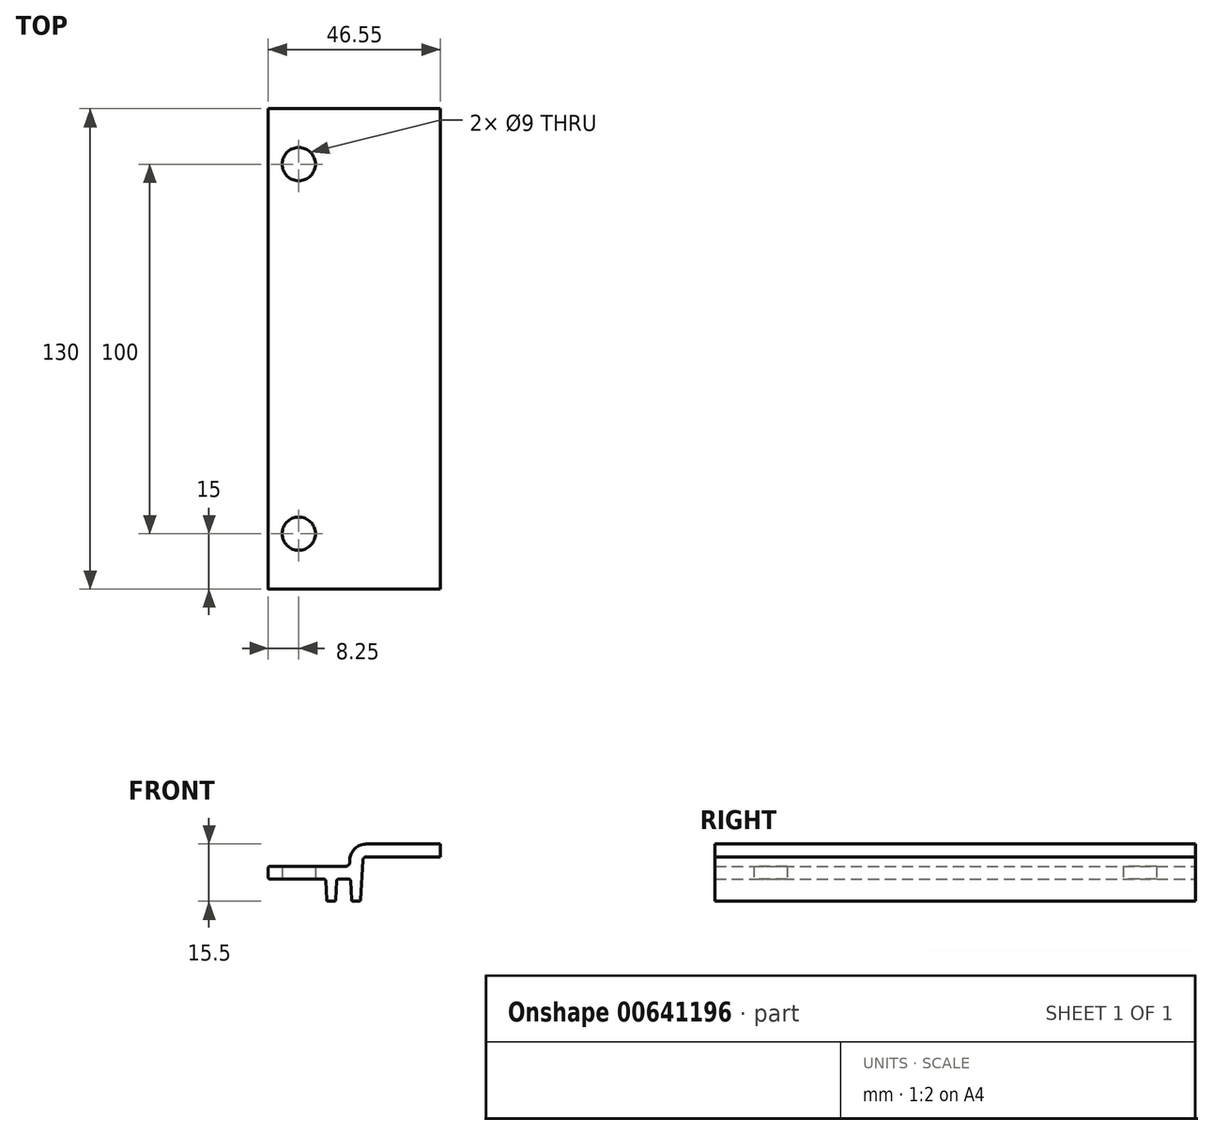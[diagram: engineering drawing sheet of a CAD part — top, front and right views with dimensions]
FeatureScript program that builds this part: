
annotation { "Feature Type Name" : "Feature", "Feature Type Description" : "" }
export const myFeature = defineFeature(function(context is Context, id is Id, definition is map)
    precondition{}
    {
        {
            var Q0;
            Q0=qCreatedBy(makeId("Front.planeOp"),FACE);
            var sketch = newSketch(context, id + "F0", { "sketchPlane" : qUnion([Q0])});
            skLineSegment(sketch, "E0", {"start": v(25.26, -0.97) * mm, "end": v(25, -6.03) * mm});
            skArc(sketch, "E1", {"start": v(24.5, -6.5) * mm, "mid": v(24.84, -6.36) * mm, "end": v(25, -6.03) * mm});
            skLineSegment(sketch, "E2", {"start": v(24.5, -6.5) * mm, "end": v(23.03, -6.5) * mm});
            skArc(sketch, "E3", {"start": v(22.53, -6.03) * mm, "mid": v(22.68, -6.36) * mm, "end": v(23.03, -6.5) * mm});
            skLineSegment(sketch, "E4", {"start": v(22.53, -6.03) * mm, "end": v(22.26, -0.97) * mm});
            skArc(sketch, "E5", {"start": v(22.26, -0.97) * mm, "mid": v(22.1, -0.64) * mm, "end": v(21.77, -0.5) * mm});
            skLineSegment(sketch, "E6", {"start": v(21.77, -0.5) * mm, "end": v(19.02, -0.5) * mm});
            skArc(sketch, "E7", {"start": v(19.02, -0.5) * mm, "mid": v(18.68, -0.64) * mm, "end": v(18.52, -0.97) * mm});
            skLineSegment(sketch, "E8", {"start": v(18.52, -0.97) * mm, "end": v(18.26, -6.03) * mm});
            skArc(sketch, "E9", {"start": v(17.76, -6.5) * mm, "mid": v(18.1, -6.36) * mm, "end": v(18.26, -6.03) * mm});
            skLineSegment(sketch, "E10", {"start": v(17.76, -6.5) * mm, "end": v(16.29, -6.5) * mm});
            skArc(sketch, "E11", {"start": v(15.79, -6.03) * mm, "mid": v(15.94, -6.36) * mm, "end": v(16.29, -6.5) * mm});
            skLineSegment(sketch, "E12", {"start": v(15.79, -6.03) * mm, "end": v(15.52, -0.97) * mm});
            skArc(sketch, "E13", {"start": v(0.5, 3) * mm, "mid": v(0.15, 2.85) * mm, "end": v(0, 2.5) * mm});
            skArc(sketch, "E14", {"start": v(15.52, -0.97) * mm, "mid": v(15.37, -0.64) * mm, "end": v(15.03, -0.5) * mm});
            skLineSegment(sketch, "E15", {"start": v(15.03, -0.5) * mm, "end": v(0.5, -0.5) * mm});
            skArc(sketch, "E16", {"start": v(0, 0) * mm, "mid": v(0.15, -0.35) * mm, "end": v(0.5, -0.5) * mm});
            skLineSegment(sketch, "E17", {"start": v(0, 2.5) * mm, "end": v(0, 0) * mm});
            skLineSegment(sketch, "E18", {"start": v(15.03, -0.5) * mm, "end": v(19.02, -0.5) * mm, "construction": true});
            skLineSegment(sketch, "E19", {"start": v(22.26, -0.97) * mm, "end": v(25.26, -0.97) * mm, "construction": true});
            skLineSegment(sketch, "E20", {"start": v(25.26, -0.97) * mm, "end": v(25.55, 4.55) * mm});
            skArc(sketch, "E21", {"start": v(26.55, 5.5) * mm, "mid": v(25.86, 5.23) * mm, "end": v(25.55, 4.55) * mm});
            skLineSegment(sketch, "E22", {"start": v(26.55, 5.5) * mm, "end": v(46.55, 5.5) * mm});
            skLineSegment(sketch, "E23", {"start": v(46.55, 5.5) * mm, "end": v(46.55, 9) * mm});
            skLineSegment(sketch, "E24", {"start": v(46.55, 9) * mm, "end": v(26.55, 9) * mm});
            skArc(sketch, "E25", {"start": v(26.55, 9) * mm, "mid": v(23.46, 7.76) * mm, "end": v(22.06, 4.74) * mm});
            skLineSegment(sketch, "E26", {"start": v(22.06, 4.74) * mm, "end": v(22.02, 3.95) * mm});
            skArc(sketch, "E27", {"start": v(21.02, 3) * mm, "mid": v(21.7, 3.27) * mm, "end": v(22.02, 3.95) * mm});
            skLineSegment(sketch, "E28", {"start": v(21.02, 3) * mm, "end": v(0.5, 3) * mm});
            skLineSegment(sketch, "E29", {"start": v(4.87, 3) * mm, "end": v(4.87, -0.5) * mm, "construction": true});
            skSolve(sketch);
        }
        {
            var Q0;
            Q0=qSketchRegion(id+"F0",true);
            extrude(context, id + "F1", {"entities" : qUnion([Q0]), "depth" : 130 * mm, "offsetDistance" : 25 * mm});
        }
        {
            var Q0;
            Q0=makeQuery(id+"F1.opExtrude","SWEPT_FACE",FACE,{"disambiguationData":[OSD([sQuery(id+"F0.wireOp",EDGE,"E15")])]});
            var sketch = newSketch(context, id + "F2", { "sketchPlane" : qUnion([Q0])});
            skLineSegment(sketch, "E30", {"start": v(0.5, 0) * mm, "end": v(18.52, 0) * mm, "construction": true});
            skPoint(sketch, "E31", {"position": v(8.25, 15) * mm});
            skPoint(sketch, "E32", {"position": v(8.25, 115) * mm});
            skLineSegment(sketch, "E33", {"start": v(8.25, 115) * mm, "end": v(0.5, 115) * mm, "construction": true});
            skLineSegment(sketch, "E34", {"start": v(8.25, 115) * mm, "end": v(8.25, 15) * mm, "construction": true});
            skSolve(sketch);
        }
        {
            var Q0;
            Q0=sQuery(id+"F2.wireOp",VERTEX,"E32");
            var Q1;
            Q1=makeQuery(id+"F1.opExtrude","SWEPT_BODY",BODY,{"disambiguationData":[OSD([sQuery(id+"F0.wireOp",EDGE,"q2KE1MzZ-A23g-frof-4Qzd-GnE8d39uKLR0"),sQuery(id+"F0.wireOp",EDGE,"mwzAUuZV-tBJK-wnh2-V2zH-PcaMI2myHO8p"),sQuery(id+"F0.wireOp",EDGE,"AJSGlvkH-hNvw-nDrQ-FQsB-ERf2I3ZEGn6d"),sQuery(id+"F0.wireOp",EDGE,"HOQ6DTzw-UcfC-E0EL-EDUk-y0muz7LuNLxK"),sQuery(id+"F0.wireOp",EDGE,"E0"),sQuery(id+"F0.wireOp",EDGE,"E1"),sQuery(id+"F0.wireOp",EDGE,"E2"),sQuery(id+"F0.wireOp",EDGE,"E3"),sQuery(id+"F0.wireOp",EDGE,"E4"),sQuery(id+"F0.wireOp",EDGE,"E5"),sQuery(id+"F0.wireOp",EDGE,"E6"),sQuery(id+"F0.wireOp",EDGE,"E7"),sQuery(id+"F0.wireOp",EDGE,"E8"),sQuery(id+"F0.wireOp",EDGE,"E9"),sQuery(id+"F0.wireOp",EDGE,"E10"),sQuery(id+"F0.wireOp",EDGE,"E11"),sQuery(id+"F0.wireOp",EDGE,"E12"),sQuery(id+"F0.wireOp",EDGE,"E13"),sQuery(id+"F0.wireOp",EDGE,"E14"),sQuery(id+"F0.wireOp",EDGE,"E15"),sQuery(id+"F0.wireOp",EDGE,"E16"),sQuery(id+"F0.wireOp",EDGE,"E17")])]});
            hole(context, id + "F3", {"style" : HoleStyle.SIMPLE, "endStyle" : HoleEndStyle.THROUGH, "holeDiameter" : 9 * mm, "majorDiameter" : 5 * mm, "isTappedThrough" : true, "tappedDepth" : 12 * mm, "tapClearance" : 3, "locations" : qUnion([Q0]), "scope" : qUnion([Q1])});
        }
        {
            var Q0;
            Q0=sQuery(id+"F2.wireOp",VERTEX,"E31");
            var Q1;
            Q1=makeQuery(id+"F1.opExtrude","SWEPT_BODY",BODY,{"disambiguationData":[OSD([sQuery(id+"F0.wireOp",EDGE,"q2KE1MzZ-A23g-frof-4Qzd-GnE8d39uKLR0"),sQuery(id+"F0.wireOp",EDGE,"mwzAUuZV-tBJK-wnh2-V2zH-PcaMI2myHO8p"),sQuery(id+"F0.wireOp",EDGE,"AJSGlvkH-hNvw-nDrQ-FQsB-ERf2I3ZEGn6d"),sQuery(id+"F0.wireOp",EDGE,"HOQ6DTzw-UcfC-E0EL-EDUk-y0muz7LuNLxK"),sQuery(id+"F0.wireOp",EDGE,"E0"),sQuery(id+"F0.wireOp",EDGE,"E1"),sQuery(id+"F0.wireOp",EDGE,"E2"),sQuery(id+"F0.wireOp",EDGE,"E3"),sQuery(id+"F0.wireOp",EDGE,"E4"),sQuery(id+"F0.wireOp",EDGE,"E5"),sQuery(id+"F0.wireOp",EDGE,"E6"),sQuery(id+"F0.wireOp",EDGE,"E7"),sQuery(id+"F0.wireOp",EDGE,"E8"),sQuery(id+"F0.wireOp",EDGE,"E9"),sQuery(id+"F0.wireOp",EDGE,"E10"),sQuery(id+"F0.wireOp",EDGE,"E11"),sQuery(id+"F0.wireOp",EDGE,"E12"),sQuery(id+"F0.wireOp",EDGE,"E13"),sQuery(id+"F0.wireOp",EDGE,"E14"),sQuery(id+"F0.wireOp",EDGE,"E15"),sQuery(id+"F0.wireOp",EDGE,"E16"),sQuery(id+"F0.wireOp",EDGE,"E17")])]});
            hole(context, id + "F4", {"style" : HoleStyle.SIMPLE, "endStyle" : HoleEndStyle.THROUGH, "holeDiameter" : 9 * mm, "majorDiameter" : 5 * mm, "isTappedThrough" : true, "tappedDepth" : 12 * mm, "tapClearance" : 3, "locations" : qUnion([Q0]), "scope" : qUnion([Q1])});
        }
    });
